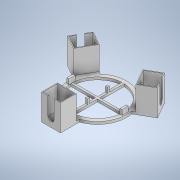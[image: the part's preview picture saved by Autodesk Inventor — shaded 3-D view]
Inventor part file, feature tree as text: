
AUTODESK INVENTOR PART (.ipt)
format: ipt  version: 2020 (Build 240168000, 168)  size: 247,808 bytes
history: native  units: mm
features: extrude x4, sketch x4, pattern_circular x1
ambient origin geometry x8: Origin, YZ Plane, XZ Plane, XY Plane, X Axis, Y Axis, Z Axis, Center Point
bodies: Solid1 (feature_tree)
feature tree (9):
  extrude  "Extrusion1"  Depth=100.0mm
  extrude  "Extrusion2"  Depth=4.0mm
  extrude  "Extrusion3"  Depth=100.0mm
  pattern_circular  "Circular Pattern1"  Count=6  [1 undecoded]
  extrude  "Extrusion4"  Depth=31.0mm
  sketch  "Sketch1"  dims[d0=114.0mm d1=100.0mm]
  sketch  "Sketch2"  dims[d6=100.0mm d7=4.0mm]
  sketch  "Sketch4"  dims[d8=4.0mm d9=100.0mm]
  sketch  "Sketch5"  dims[d10=37.0mm d14=60.0mm d15=31.0mm d16=30.0mm d18=360.0deg d20=5.0mm d21=0.0mm d22=31.0mm d23=1.5mm d24=30.0mm d26=360.0deg d28=46.0mm d29=0.0mm d30=30.0mm d31=360.0deg d36=12.0mm d37=5.0mm d38=6.0mm d39=46.0mm d40=0.0mm d41=17.5mm d42=4.0mm d43=12.0mm d44=10.0mm d45=0.0mm]
note: 1 required parameter value undecoded (feature->parameter linkage not recoverable at this tier; creation-order binding heuristic only, values carry confidence <= 0.55)
